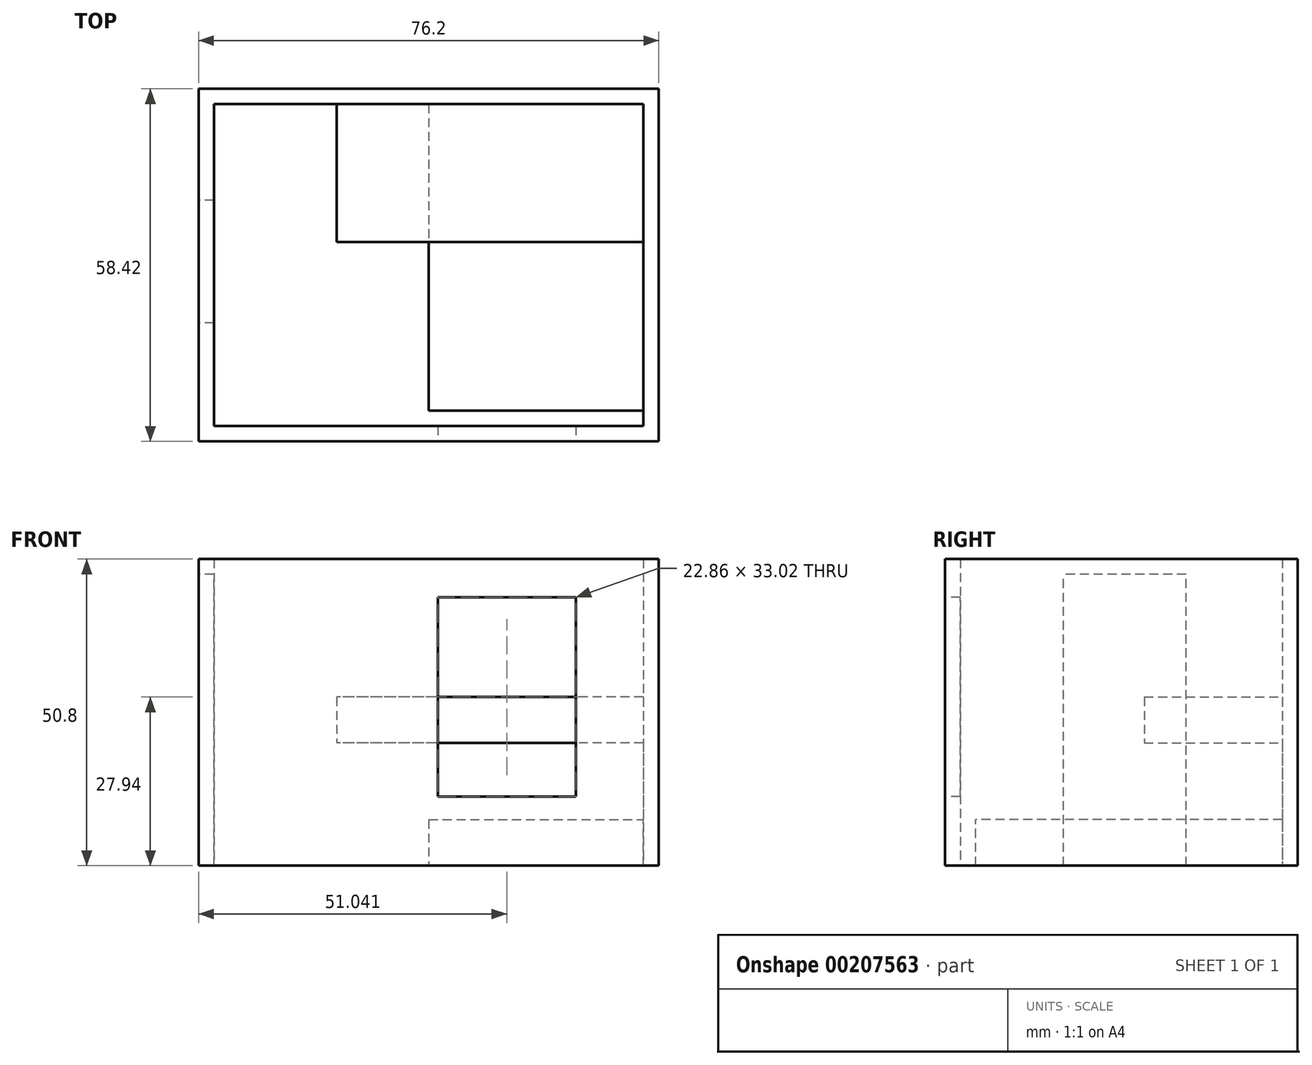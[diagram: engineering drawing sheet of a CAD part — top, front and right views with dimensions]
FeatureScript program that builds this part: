
annotation { "Feature Type Name" : "Feature", "Feature Type Description" : "" }
export const myFeature = defineFeature(function(context is Context, id is Id, definition is map)
    precondition{}
    {
        {
            var Q0;
            Q0=qCreatedBy(makeId("Top.planeOp"),FACE);
            var sketch = newSketch(context, id + "F0", { "sketchPlane" : qUnion([Q0])});
            skLineSegment(sketch, "E0.bottom", {"start": v(-6.74, 14.27) * mm, "end": v(69.46, 14.27) * mm});
            skLineSegment(sketch, "E0.top", {"start": v(-6.74, -44.15) * mm, "end": v(69.46, -44.15) * mm});
            skLineSegment(sketch, "E0.left", {"start": v(-6.74, 14.27) * mm, "end": v(-6.74, -44.15) * mm});
            skLineSegment(sketch, "E0.right", {"start": v(69.46, 14.27) * mm, "end": v(69.46, -44.15) * mm});
            skLineSegment(sketch, "E1.bottom", {"start": v(-4.2, 11.73) * mm, "end": v(66.92, 11.73) * mm});
            skLineSegment(sketch, "E1.top", {"start": v(-4.2, -41.61) * mm, "end": v(66.92, -41.61) * mm});
            skLineSegment(sketch, "E1.left", {"start": v(-4.2, 11.73) * mm, "end": v(-4.2, -41.61) * mm});
            skLineSegment(sketch, "E1.right", {"start": v(66.92, 11.73) * mm, "end": v(66.92, -41.61) * mm});
            skLineSegment(sketch, "E2", {"start": v(4.94, 14.27) * mm, "end": v(4.94, 11.73) * mm, "construction": true});
            skLineSegment(sketch, "E3", {"start": v(-6.74, -28.07) * mm, "end": v(-4.2, -28.07) * mm, "construction": true});
            skLineSegment(sketch, "E4", {"start": v(4.5, -44.15) * mm, "end": v(4.5, -41.61) * mm, "construction": true});
            skLineSegment(sketch, "E5", {"start": v(66.92, -14.94) * mm, "end": v(69.46, -14.94) * mm, "construction": true});
            skSolve(sketch);
        }
        {
            var Q0;
            Q0=makeQuery(id+"F0.imprint","IMPRINT",FACE,{"disambiguationData":[TD([[makeQuery(id+"F0.imprint","IMPRINT",EDGE,{"derivedFrom":sQuery(id+"F0.wireOp",EDGE,"E0.bottom")}),-1.0]])]});
            extrude(context, id + "F1", {"entities" : qUnion([Q0]), "depth" : 50.8 * mm});
        }
        {
            var Q0;
            Q0=makeQuery(id+"F1.opExtrude","SWEPT_FACE",FACE,{"disambiguationData":[OSD([sQuery(id+"F0.wireOp",EDGE,"E1.bottom")])]});
            var sketch = newSketch(context, id + "F2", { "sketchPlane" : qUnion([Q0])});
            skLineSegment(sketch, "E6.bottom", {"start": v(66.92, 27.94) * mm, "end": v(16.12, 27.94) * mm});
            skLineSegment(sketch, "E6.top", {"start": v(66.92, 20.32) * mm, "end": v(16.12, 20.32) * mm});
            skLineSegment(sketch, "E6.left", {"start": v(66.92, 27.94) * mm, "end": v(66.92, 20.32) * mm});
            skLineSegment(sketch, "E6.right", {"start": v(16.12, 27.94) * mm, "end": v(16.12, 20.32) * mm});
            skSolve(sketch);
        }
        {
            var Q0;
            Q0=makeQuery(id+"F2.imprint","IMPRINT",FACE,{"disambiguationData":[TD([[makeQuery(id+"F2.imprint","IMPRINT",EDGE,{"derivedFrom":sQuery(id+"F2.wireOp",EDGE,"E6.bottom")}),1.0]])]});
            extrude(context, id + "F6", {"entities" : qUnion([Q0]), "operationType" : NewBodyOperationType.ADD, "depth" : 22.86 * mm});
        }
        {
            var Q0;
            Q0=makeQuery(id+"F1.opExtrude","SWEPT_FACE",FACE,{"disambiguationData":[OSD([sQuery(id+"F0.wireOp",EDGE,"E1.right")])]});
            var sketch = newSketch(context, id + "F7", { "sketchPlane" : qUnion([Q0])});
            skLineSegment(sketch, "E7.bottom", {"start": v(-11.73, 0) * mm, "end": v(39.07, 0) * mm});
            skLineSegment(sketch, "E7.top", {"start": v(-11.73, 7.62) * mm, "end": v(39.07, 7.62) * mm});
            skLineSegment(sketch, "E7.left", {"start": v(-11.73, 0) * mm, "end": v(-11.73, 7.62) * mm});
            skLineSegment(sketch, "E7.right", {"start": v(39.07, 0) * mm, "end": v(39.07, 7.62) * mm});
            skSolve(sketch);
        }
        {
            var Q0;
            Q0=makeQuery(id+"F7.imprint","IMPRINT",FACE,{"disambiguationData":[TD([[makeQuery(id+"F7.imprint","IMPRINT",EDGE,{"derivedFrom":sQuery(id+"F7.wireOp",EDGE,"E7.bottom")}),1.0]])]});
            extrude(context, id + "F8", {"entities" : qUnion([Q0]), "operationType" : NewBodyOperationType.ADD, "depth" : 35.56 * mm});
        }
        {
            var Q0;
            Q0=makeQuery(id+"F1.opExtrude","SWEPT_FACE",FACE,{"disambiguationData":[OSD([sQuery(id+"F0.wireOp",EDGE,"E0.left")])]});
            var sketch = newSketch(context, id + "F3", { "sketchPlane" : qUnion([Q0])});
            skLineSegment(sketch, "E8.bottom", {"start": v(4.21, 0) * mm, "end": v(24.53, 0) * mm});
            skLineSegment(sketch, "E8.top", {"start": v(4.21, 48.26) * mm, "end": v(24.53, 48.26) * mm});
            skLineSegment(sketch, "E8.left", {"start": v(4.21, 0) * mm, "end": v(4.21, 48.26) * mm});
            skLineSegment(sketch, "E8.right", {"start": v(24.53, 0) * mm, "end": v(24.53, 48.26) * mm});
            skSolve(sketch);
        }
        {
            var Q0;
            Q0=makeQuery(id+"F3.imprint","IMPRINT",FACE,{"disambiguationData":[TD([[makeQuery(id+"F3.imprint","IMPRINT",EDGE,{"derivedFrom":sQuery(id+"F3.wireOp",EDGE,"E8.bottom")}),1.0]])]});
            extrude(context, id + "F9", {"entities" : qUnion([Q0]), "operationType" : NewBodyOperationType.REMOVE, "endBound" : BoundingType.UP_TO_NEXT, "oppositeDirection" : true, "depth" : 25.4 * mm});
        }
        {
            var Q0;
            Q0=makeQuery(id+"F1.opExtrude","SWEPT_FACE",FACE,{"disambiguationData":[OSD([sQuery(id+"F0.wireOp",EDGE,"E0.top")])]});
            var sketch = newSketch(context, id + "F4", { "sketchPlane" : qUnion([Q0])});
            skLineSegment(sketch, "E9.bottom", {"start": v(32.87, 11.43) * mm, "end": v(55.73, 11.43) * mm});
            skLineSegment(sketch, "E9.top", {"start": v(32.87, 44.45) * mm, "end": v(55.73, 44.45) * mm});
            skLineSegment(sketch, "E9.left", {"start": v(32.87, 11.43) * mm, "end": v(32.87, 44.45) * mm});
            skLineSegment(sketch, "E9.right", {"start": v(55.73, 11.43) * mm, "end": v(55.73, 44.45) * mm});
            skSolve(sketch);
        }
        {
            var Q0;
            Q0=makeQuery(id+"F4.imprint","IMPRINT",FACE,{"disambiguationData":[TD([[makeQuery(id+"F4.imprint","IMPRINT",EDGE,{"derivedFrom":sQuery(id+"F4.wireOp",EDGE,"E9.bottom")}),1.0]])]});
            extrude(context, id + "F5", {"entities" : qUnion([Q0]), "operationType" : NewBodyOperationType.REMOVE, "endBound" : BoundingType.UP_TO_NEXT, "oppositeDirection" : true, "depth" : 25.4 * mm});
        }
    });
